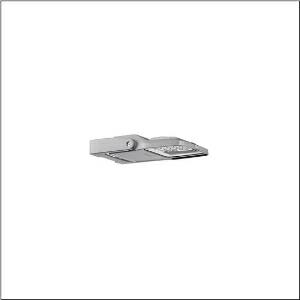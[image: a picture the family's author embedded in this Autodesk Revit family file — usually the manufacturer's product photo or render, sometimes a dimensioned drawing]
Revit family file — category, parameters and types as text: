
# Revit family: floodlight_fl_21_iq_micro___pl64_5xa7761a2e2a_9d46
name_source: partatom
category: Lighting Fixtures
units: mm (PartAtom-declared; Revit-internal decimal feet)

## family parameters
Cut with Voids When Loaded = No
Host = Face
Light Source = No
Part Type = Normal
Room Calculation Point = No
Round Connector Dimension = Use Diameter
Shared = No

## types (1)
- --- (1 x LED, 2870 lm, 23.1 W, 3000K)
    Apparent Load = 23 VA
    CIE Flux Codes = 28 80 98 100 100
    Color Rendering = 70
    Color Temperature = 3000K
    Default Elevation = 1800 mm
    Description = Floodlight FL 21 iQ micro, floodlight, primary light control with lens, of PMMA, primary optical cover: protective disc, of toughened safety glass, transparent, light distribution: PL64, light emission: direct distribution, installation type: surface-mounted, lamps: LED, High Power LED, rated values: 2.870lm | 23,1W | 124,2lm/W (begin service life); end service life: 2.870lm | 23,8W; at 50% lumin. flux: 1.435lm | 11W | 130,5lm/W, colour temperature: 3000K, colour rendering: CRI > 70, light colour: 730, light setting 1 begin service life: 100% | 2.870lm | 23,1W | 124,2lm/W | 3.000K, light setting 1 end service life: 23,8W, further light settings possible, control: optimised constant luminous flux control (CLO 2.0), Desk-Remote (wireless, voltage-free reading and setting of iQ features in the workshop via application-optimized NFC function/RFID function), Light-Fading, Smart-Wire, Night-Set, Lumen-Switch, Temp-Guard, Auto-Match, pre-setting: linear dimming characteristic, with terminal, 6-pole, mains connection: 220..240V, AC, 50/60Hz, luminaire housing, of diecast aluminium, powder-coated, SITECO metallic grey (DB 702S), corrosivity category C5 mid according to DIN EN ISO 12944suitable for swimming poolschlorine-resistant, sealing non-destructively replaceable, design bracket, of diecast aluminium, powder-coated, SITECO metallic grey (DB 702S), protection rating (complete): IP66, insulation class (complete): insulation class II (safety insulation), certification: CE, ENEC, VDE, protection symbol: D, impact resistance: IK07, permissible operating ambient temperature: -40..+40°C, permissible operating ambient temperature for outdoor applications: -40..+50°C, standard: DIN EN 12944, LABS conformity tested according to VDMA 24364:2018-05, packaging unit: 1 piece

Light Distribution: PL64
    Height = 65 mm
    Lamp = 1 x LED
    Lamp Light Flux = 2870 lm
    Lamp Power = 23.1 W
    Lamp count = 1
    Length = 312 mm
    Luminous efficacy = 124 lm/W
    Manufacturer = Siteco
    ModVariant = No
    Model = 5XA7761A2E2A
    Mounting Place = Wall
    Mounting Type = Surface mounted
    Number of Poles = 1
    OnlyDefault = Yes
    Power Factor = 1
    Product Name = Floodlight FL 21 iQ micro | PL64
    Product group = floodlight | wall mounted
    ProductGroupID = 2002
    Protection Class = Protection class II
    Protection Degree = IP 66
    RLX_Detail_Level = 1
    RLX_Emergency_Light_Flux = 0 lm
    RLX_Emergency_Type = 0
    RLX_Emergency_Type_DB = No
    RlxData = <blob elided: 97621 chars, md5=2dfdf17c>
    Socket = socket
    Standby Power = 0 W
    System Light Flux = 2870 lm
    System Power = 23 W
    Type Comments = factory setting: luminous flux: 100 % | dim-lin: 254 | 455 mA
    Type Image = l_1006878.jpg
    URL = http://relux.com
    VarID = @adj_179633
    Voltage = 0 V
    Weight = 0.00 kg
    Width = 230 mm

## geometry (parser evidence)
native form markers: Blend x4, Sweep x12
no freeform markers — native parametric forms only
